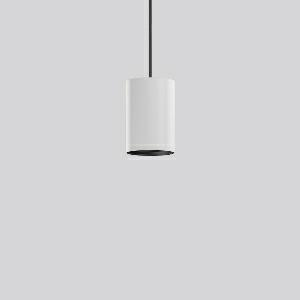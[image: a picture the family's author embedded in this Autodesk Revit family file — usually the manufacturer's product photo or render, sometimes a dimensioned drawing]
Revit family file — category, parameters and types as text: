
# Revit family: deecos_p_maxi_911544_002_76_5d3c
name_source: partatom
category: Lighting Fixtures
units: mm (PartAtom-declared; Revit-internal decimal feet)

## family parameters
Cut with Voids When Loaded = No
Host = Face
Light Source = No
Part Type = Normal
Room Calculation Point = No
Round Connector Dimension = Use Diameter
Shared = No

## types (1)
- DEECOS P maxi (1 x LED Modul 932 fresh meat, 2150 lm, 3200)
    Apparent Load = 33 VA
    Approval mark = CE
    CIE Flux Codes = 100 100 100 100 100
    Color Rendering = 90
    Color Temperature = 3200
    Default Elevation = 1800 mm
    Description = Series: DEECOS P maxi
Cylindrical pendant luminaire. Housing: die-cast aluminium, powder-coated. Canopy made of powder-coated sheet steel with magnetic attachment. Optical assembly with reflector made of MIRO-Silver with 98% total light reflection for outstanding efficiency - can be changed without tools. Including special LED for illuminating meat products / Meat fresh - reddish white. Transparent suspension cable 2 m, can be shortened. High quality converter without flickering and stroboscopic effect. The following accessories can be mounted without use of tools: interchangeable lenses, honeycomb louvre, clear and frosted diffusers, white interchangeable plastic ring. Decorative recessed suspension set available as accessory. 
Colour: traffic white, matt (RAL 9016)
Diameter: 123 mm
Height: 181 mm
Suspension length: 2000 mm
Lamp: LED
Socket: without socket
Colour temperature: fresh meat
Colour rendering index (CRI): 92
System power: 33 W
Rated luminous flux: 2150 lm
Luminous efficiency: 65 lm/W
Control gear: Converter, dimmable, DALI
Protection class: I
Type of protection: IP 20
    Height = 181 mm
    Lamp = 1 x LED Modul 932 fresh meat
    Lamp Light Flux = 2150 lm
    Lamp count = 1
    Length = 123 mm
    Lifetime = 50000 h
    Luminous efficacy = 65 lm/W
    Manufacturer = RZB
    ModVariant = No
    Model = 911544.002.76
    Mounting Place = Ceiling
    Mounting Type = Pendant
    Number of Poles = 1
    OnlyDefault = Yes
    Power Factor = 1
    Product Name = DEECOS P maxi
    Product group = Pendant luminaires
    ProductGroupID = 902
    Protection Class = Protection class I
    Protection Degree = IP 20
    RLX_Detail_Level = 1
    RLX_Emergency_Light_Flux = 0 lm
    RLX_Emergency_Type = 0
    RLX_Emergency_Type_DB = No
    RlxData = <blob elided: 35885 chars, md5=c6c4956b>
    Socket = socket
    Standby Power = 0 W
    System Light Flux = 2150 lm
    System Power = 33 W
    Type Comments = Product without accessories
    Type Image = 911480.002.jpg
    URL = http://relux.com
    VarID = ---
    Voltage = 230 V
    Voltage Range = 220-240 V
    Weight = 0.00 kg
    Width = 0 mm  [stored 0 ft]

note: [stored X ft] marks values corroborated as IEEE doubles in the binary element streams (Revit-internal decimal feet)

## geometry (parser evidence)
native form markers: Blend x4, Sweep x10
no freeform markers — native parametric forms only
